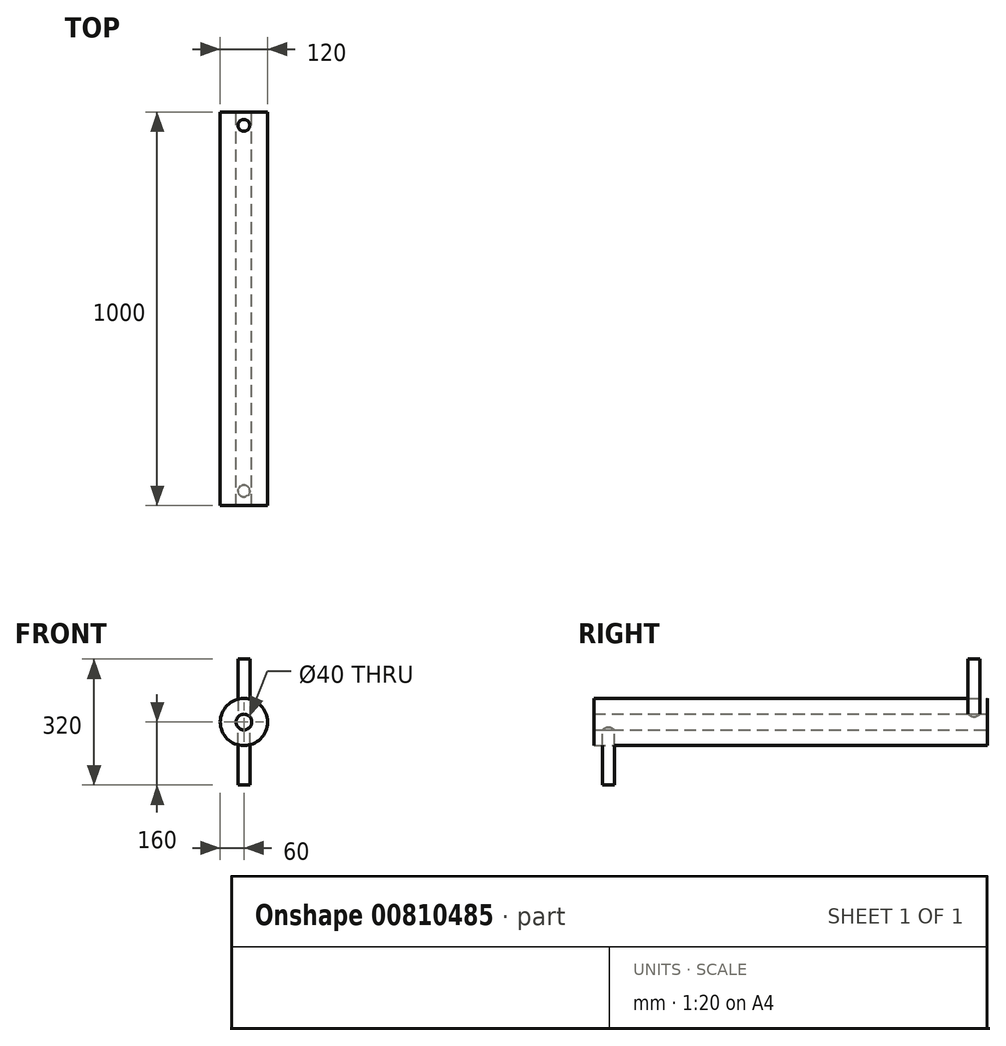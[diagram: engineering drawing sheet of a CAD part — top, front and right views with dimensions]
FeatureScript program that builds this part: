
annotation { "Feature Type Name" : "Feature", "Feature Type Description" : "" }
export const myFeature = defineFeature(function(context is Context, id is Id, definition is map)
    precondition{}
    {
        {
            var Q0;
            Q0=qCreatedBy(makeId("Front.planeOp"),FACE);
            var sketch = newSketch(context, id + "F0", { "sketchPlane" : qUnion([Q0])});
            skCircle(sketch, "E0", {"center": v(0, 0) * mm, "radius": 60 * mm});
            skSolve(sketch);
        }
        {
            var Q0;
            Q0=qCreatedBy(makeId("Front.planeOp"),FACE);
            var sketch = newSketch(context, id + "F1", { "sketchPlane" : qUnion([Q0])});
            skCircle(sketch, "E1", {"center": v(0, 0) * mm, "radius": 20 * mm});
            skSolve(sketch);
        }
        {
            var Q0;
            Q0=makeQuery(id+"F0.imprint","IMPRINT",FACE,{"disambiguationData":[TD([[makeQuery(id+"F0.imprint","IMPRINT",EDGE,{"derivedFrom":sQuery(id+"F0.wireOp",EDGE,"E0")}),1.0]])]});
            extrude(context, id + "F2", {"entities" : qUnion([Q0]), "depth" : 1000 * mm, "offsetDistance" : 25 * mm});
        }
        {
            var Q0;
            Q0=qCreatedBy(makeId("Top.planeOp"),FACE);
            var sketch = newSketch(context, id + "F3", { "sketchPlane" : qUnion([Q0])});
            skCircle(sketch, "E2", {"center": v(0, -33.89) * mm, "radius": 15 * mm});
            skSolve(sketch);
        }
        {
            var Q0;
            Q0=qSketchRegion(id+"F3",true);
            extrude(context, id + "F4", {"entities" : qUnion([Q0]), "depth" : 160 * mm, "offsetDistance" : 25 * mm});
        }
        {
            var Q0;
            Q0=qCreatedBy(makeId("Top.planeOp"),FACE);
            var sketch = newSketch(context, id + "F5", { "sketchPlane" : qUnion([Q0])});
            skCircle(sketch, "E3", {"center": v(0, -962.96) * mm, "radius": 15 * mm});
            skSolve(sketch);
        }
        {
            var Q0;
            Q0=qSketchRegion(id+"F5",true);
            extrude(context, id + "F6", {"entities" : qUnion([Q0]), "oppositeDirection" : true, "depth" : 160 * mm, "offsetDistance" : 25 * mm});
        }
        {
            var Q0;
            Q0=qSketchRegion(id+"F1",true);
            var Q1;
            Q1=sQuery(id+"F1.wireOp",EDGE,"E1");
            extrude(context, id + "F7", {"entities" : qUnion([Q0]), "operationType" : NewBodyOperationType.REMOVE, "surfaceEntities" : qUnion([Q1]), "depth" : 1000 * mm, "offsetDistance" : 25 * mm});
        }
    });
